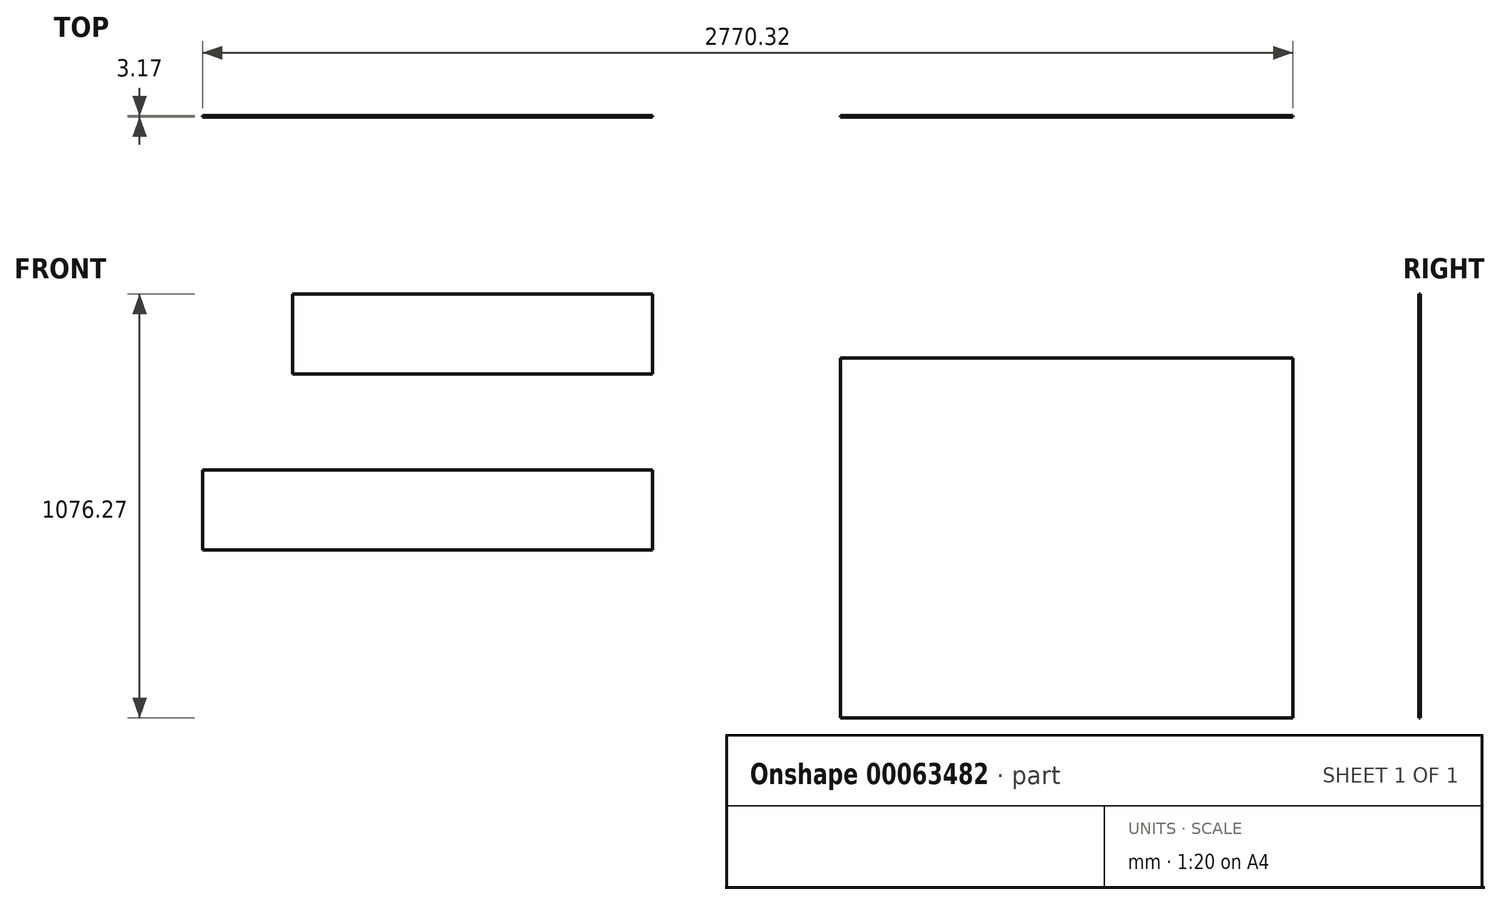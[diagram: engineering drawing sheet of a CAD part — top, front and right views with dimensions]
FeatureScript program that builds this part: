
annotation { "Feature Type Name" : "Feature", "Feature Type Description" : "" }
export const myFeature = defineFeature(function(context is Context, id is Id, definition is map)
    precondition{}
    {
        {
            var Q0;
            Q0=qCreatedBy(makeId("Front.planeOp"),FACE);
            var sketch = newSketch(context, id + "F0", { "sketchPlane" : qUnion([Q0])});
            skLineSegment(sketch, "E0.bottom", {"start": v(-985.25, 446.5) * mm, "end": v(-70.85, 446.5) * mm});
            skLineSegment(sketch, "E0.top", {"start": v(-985.25, 243.3) * mm, "end": v(-70.85, 243.3) * mm});
            skLineSegment(sketch, "E0.left", {"start": v(-985.25, 446.5) * mm, "end": v(-985.25, 243.3) * mm});
            skLineSegment(sketch, "E0.right", {"start": v(-70.85, 446.5) * mm, "end": v(-70.85, 243.3) * mm});
            skLineSegment(sketch, "E1.bottom", {"start": v(-1213.85, 0) * mm, "end": v(-70.85, 0) * mm});
            skLineSegment(sketch, "E1.top", {"start": v(-1213.85, -203.2) * mm, "end": v(-70.85, -203.2) * mm});
            skLineSegment(sketch, "E1.left", {"start": v(-1213.85, 0) * mm, "end": v(-1213.85, -203.2) * mm});
            skLineSegment(sketch, "E1.right", {"start": v(-70.85, 0) * mm, "end": v(-70.85, -203.2) * mm});
            skLineSegment(sketch, "E2.bottom", {"start": v(407.12, 284.64) * mm, "end": v(1556.47, 284.64) * mm});
            skLineSegment(sketch, "E2.top", {"start": v(407.12, -629.76) * mm, "end": v(1556.47, -629.76) * mm});
            skLineSegment(sketch, "E2.left", {"start": v(407.12, 284.64) * mm, "end": v(407.12, -629.76) * mm});
            skLineSegment(sketch, "E2.right", {"start": v(1556.47, 284.64) * mm, "end": v(1556.47, -629.76) * mm});
            skSolve(sketch);
        }
        {
            var Q0;
            Q0=makeQuery(id+"F0.imprint","IMPRINT",FACE,{"disambiguationData":[TD([[makeQuery(id+"F0.imprint","IMPRINT",EDGE,{"derivedFrom":sQuery(id+"F0.wireOp",EDGE,"E0.bottom")}),-1.0]])]});
            var Q1;
            Q1=makeQuery(id+"F0.imprint","IMPRINT",FACE,{"disambiguationData":[TD([[makeQuery(id+"F0.imprint","IMPRINT",EDGE,{"derivedFrom":sQuery(id+"F0.wireOp",EDGE,"E1.bottom")}),-1.0]])]});
            var Q2;
            Q2=makeQuery(id+"F0.imprint","IMPRINT",FACE,{"disambiguationData":[TD([[makeQuery(id+"F0.imprint","IMPRINT",EDGE,{"derivedFrom":sQuery(id+"F0.wireOp",EDGE,"E2.bottom")}),-1.0]])]});
            extrude(context, id + "F1", {"entities" : qUnion([Q0, Q1, Q2]), "depth" : 3.17 * mm});
        }
    });
